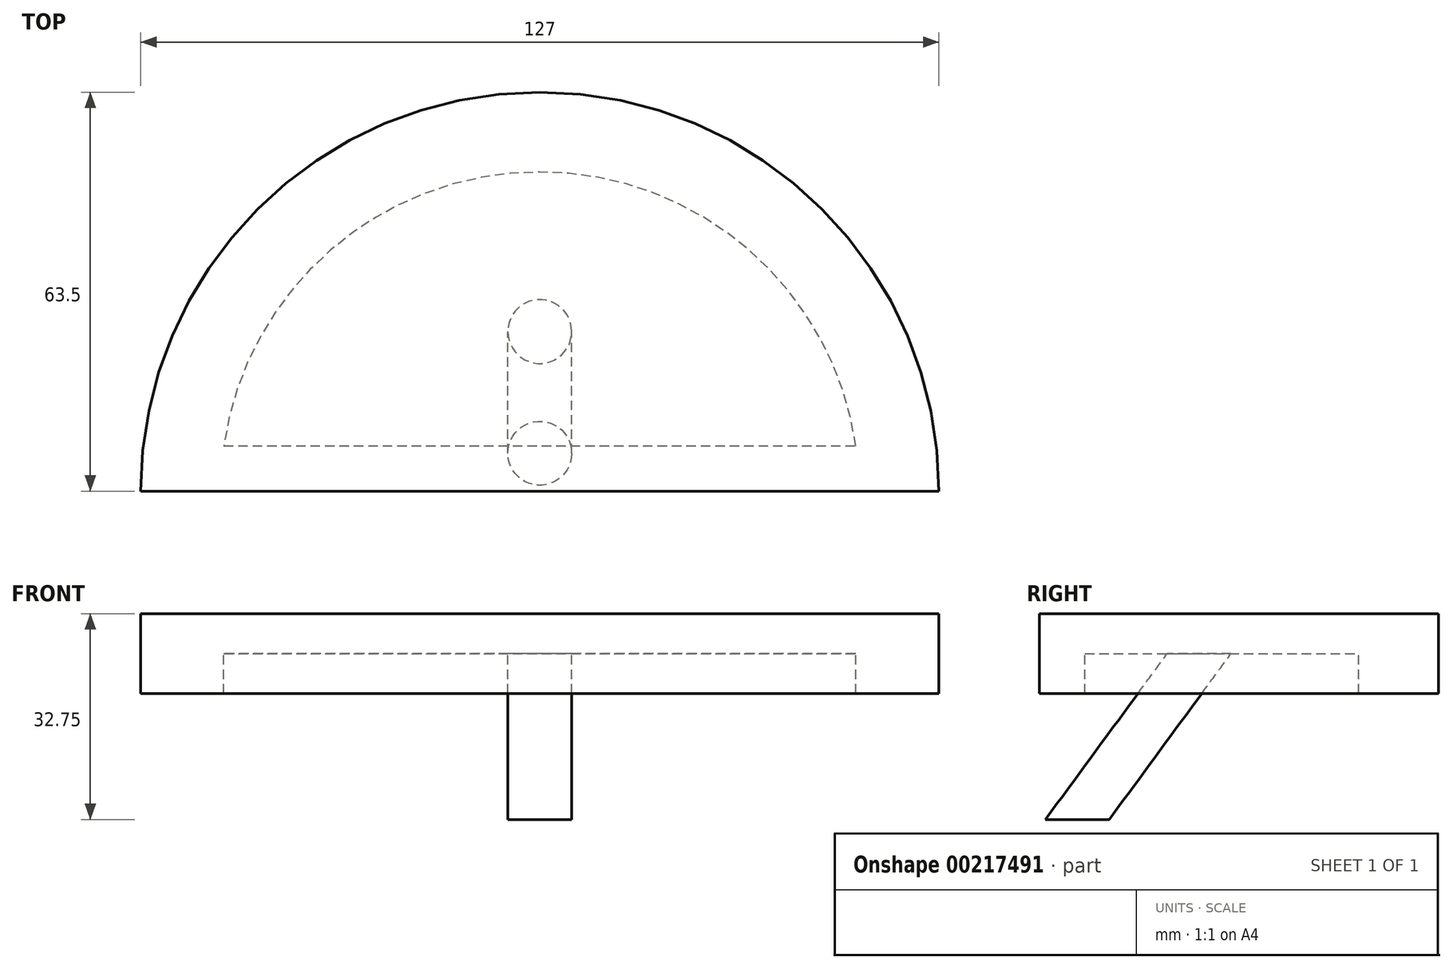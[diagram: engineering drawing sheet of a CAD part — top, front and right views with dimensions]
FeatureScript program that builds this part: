
annotation { "Feature Type Name" : "Feature", "Feature Type Description" : "" }
export const myFeature = defineFeature(function(context is Context, id is Id, definition is map)
    precondition{}
    {
        {
            var Q0;
            Q0=qCreatedBy(makeId("Top.planeOp"),FACE);
            var sketch = newSketch(context, id + "F0", { "sketchPlane" : qUnion([Q0])});
            skArc(sketch, "E0", {"start": v(63.5, 0) * mm, "mid": v(0, 63.5) * mm, "end": v(-63.5, 0) * mm});
            skLineSegment(sketch, "E1", {"start": v(-63.5, 0) * mm, "end": v(63.5, 0) * mm});
            skSolve(sketch);
        }
        {
            var Q0;
            Q0 = qSketchRegion(id + "F0", true);
            extrude(context, id + "F1", {"entities" : qUnion([Q0]), "endBound" : BoundingType.SYMMETRIC, "depth" : 12.7 * mm});
        }
        {
            var Q0;
            Q0=qCreatedBy(makeId("Top.planeOp"),FACE);
            var sketch = newSketch(context, id + "F2", { "sketchPlane" : qUnion([Q0])});
            skArc(sketch, "E2", {"start": v(50.28, 7.22) * mm, "mid": v(0, 50.8) * mm, "end": v(-50.28, 7.22) * mm});
            skLineSegment(sketch, "E3", {"start": v(-50.28, 7.22) * mm, "end": v(50.28, 7.22) * mm});
            skSolve(sketch);
        }
        {
            var Q0;
            Q0 = qSketchRegion(id + "F2", true);
            extrude(context, id + "F3", {"entities" : qUnion([Q0]), "operationType" : NewBodyOperationType.REMOVE, "oppositeDirection" : true, "depth" : 25.4 * mm});
        }
        {
            var Q0;
            Q0=qCreatedBy(makeId("Top.planeOp"),FACE);
            var sketch = newSketch(context, id + "F4", { "sketchPlane" : qUnion([Q0])});
            skCircle(sketch, "E4", {"center": v(0, 25.4) * mm, "radius": 3.81 * mm});
            skSolve(sketch);
        }
        {
            var Q0;
            Q0=qCreatedBy(makeId("Right.planeOp"),FACE);
            var sketch = newSketch(context, id + "F5", { "sketchPlane" : qUnion([Q0])});
            skLineSegment(sketch, "E5", {"start": v(25.54, 0) * mm, "end": v(6.17, -26.4) * mm});
            skSolve(sketch);
        }
        {
            var Q0;
            Q0 = qSketchRegion(id + "F4", true);
            var Q1;
            Q1 = qConstructionFilter(qBodyType(qCreatedBy(id + "F5" ,EDGE), BodyType.WIRE), ConstructionObject.NO);
            sweep(context, id + "F6", {"operationType" : NewBodyOperationType.REMOVE, "profiles" : qUnion([Q0]), "path" : qUnion([Q1])});
        }
        {
            var Q0;
            Q0=qCreatedBy(makeId("Top.planeOp"),FACE);
            var sketch = newSketch(context, id + "F7", { "sketchPlane" : qUnion([Q0])});
            skCircle(sketch, "E6", {"center": v(0, 25.4) * mm, "radius": 5.08 * mm});
            skSolve(sketch);
        }
        {
            var Q0;
            Q0 = qSketchRegion(id + "F7", true);
            var Q1;
            Q1 = qConstructionFilter(qBodyType(qCreatedBy(id + "F5" ,EDGE), BodyType.WIRE), ConstructionObject.NO);
            sweep(context, id + "F8", {"operationType" : NewBodyOperationType.ADD, "profiles" : qUnion([Q0]), "path" : qUnion([Q1])});
        }
    });
